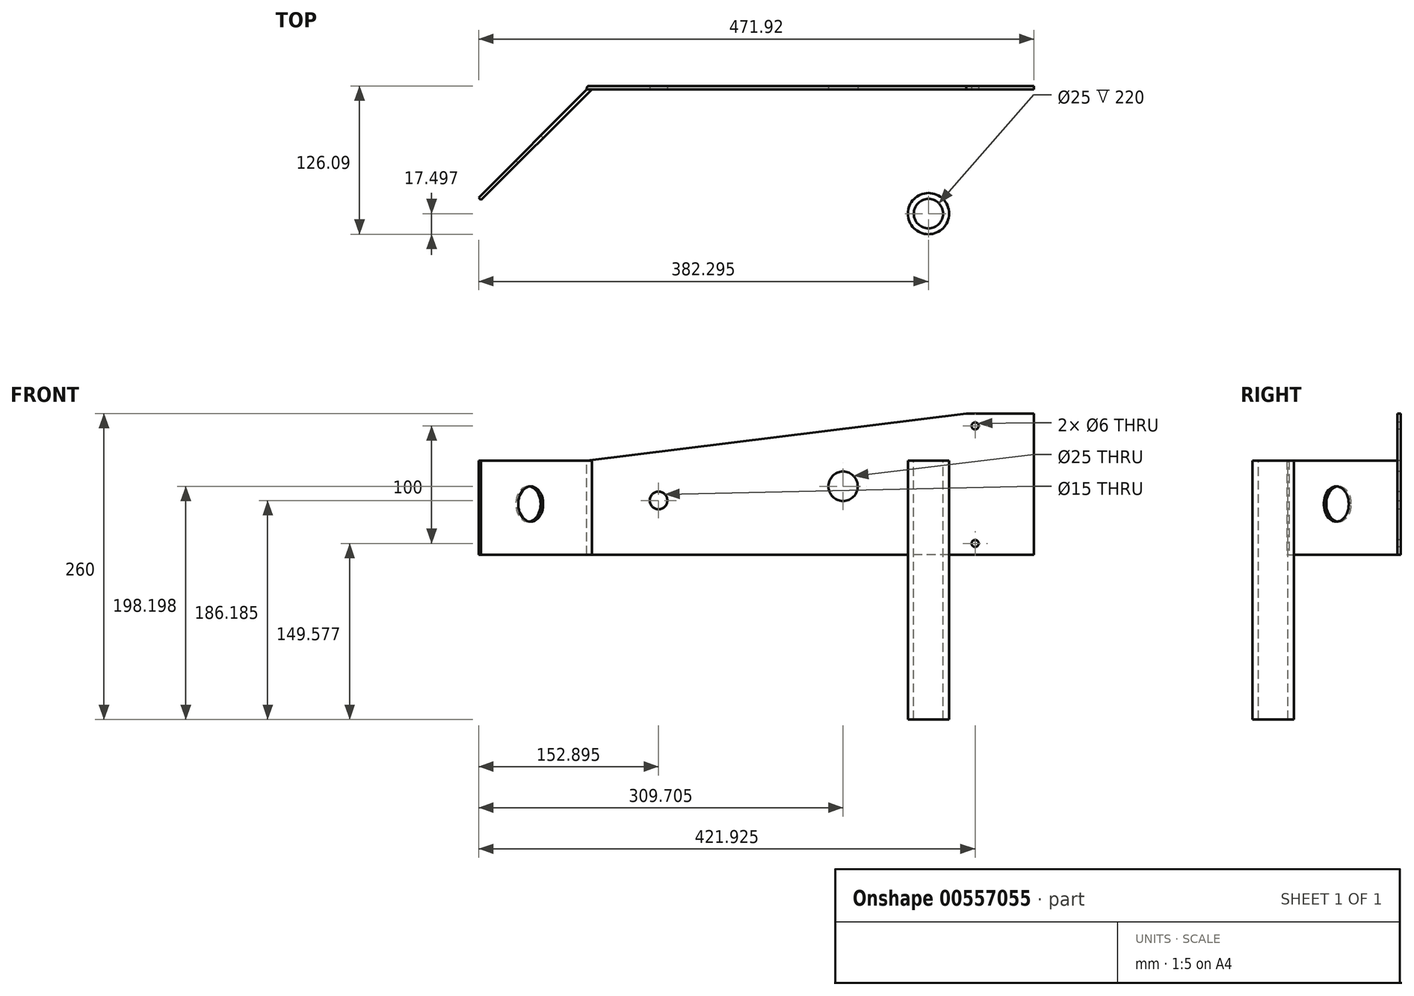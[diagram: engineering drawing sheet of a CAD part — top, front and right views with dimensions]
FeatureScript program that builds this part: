
annotation { "Feature Type Name" : "Feature", "Feature Type Description" : "" }
export const myFeature = defineFeature(function(context is Context, id is Id, definition is map)
    precondition{}
    {
        {
            var Q0;
            Q0=qCreatedBy(makeId("Front.planeOp"),FACE);
            var sketch = newSketch(context, id + "F0", { "sketchPlane" : qUnion([Q0])});
            skLineSegment(sketch, "E0.bottom", {"start": v(286.31, -3.5) * mm, "end": v(-93.69, -3.5) * mm});
            skLineSegment(sketch, "E0.top", {"start": v(286.31, 116.5) * mm, "end": v(228.84, 116.5) * mm});
            skLineSegment(sketch, "E0.left", {"start": v(286.31, -3.5) * mm, "end": v(286.31, 116.5) * mm});
            skLineSegment(sketch, "E0.right", {"start": v(-93.69, -3.5) * mm, "end": v(-93.69, 76.5) * mm});
            skLineSegment(sketch, "E1", {"start": v(-93.69, 76.5) * mm, "end": v(228.84, 116.5) * mm});
            skSolve(sketch);
        }
        {
            var Q0;
            Q0=makeQuery(id+"F0.imprint","IMPRINT",FACE,{"disambiguationData":[TD([[makeQuery(id+"F0.imprint","IMPRINT",EDGE,{"derivedFrom":sQuery(id+"F0.wireOp",EDGE,"E0.bottom")}),-1.0]])]});
            extrude(context, id + "F1", {"entities" : qUnion([Q0]), "depth" : 3 * mm, "offsetDistance" : 25 * mm});
        }
        {
            var Q0;
            Q0=makeQuery(id+"F1.opExtrude","SWEPT_FACE",FACE,{"disambiguationData":[OSD([sQuery(id+"F0.wireOp",EDGE,"E0.bottom")])]});
            var sketch = newSketch(context, id + "F2", { "sketchPlane" : qUnion([Q0])});
            skLineSegment(sketch, "E2", {"start": v(-93.69, 3) * mm, "end": v(-185.6, 94.92) * mm});
            skLineSegment(sketch, "E3", {"start": v(-185.6, 94.92) * mm, "end": v(-183.49, 97.05) * mm});
            skLineSegment(sketch, "E4", {"start": v(-183.49, 97.05) * mm, "end": v(-86.44, 0) * mm});
            skLineSegment(sketch, "E5", {"start": v(-93.69, 3) * mm, "end": v(-217, 3) * mm, "construction": true});
            skSolve(sketch);
        }
        {
            var Q0;
            {var subQ0=sQuery(id+"F2.wireOp",EDGE,"E2");Q0=makeQuery(id+"F2.imprint","IMPRINT",FACE,{"disambiguationData":[TD([[makeQuery(id+"F2.imprint","IMPRINT",EDGE,{"derivedFrom":subQ0}),-1.0]])]});}
            var sketch = newSketch(context, id + "F3", { "sketchPlane" : qUnion([Q0])});
            skSolve(sketch);
        }
        {
            var Q0;
            {var subQ0=sQuery(id+"F2.wireOp",EDGE,"E2");Q0=makeQuery(id+"F2.imprint","IMPRINT",FACE,{"disambiguationData":[TD([[makeQuery(id+"F2.imprint","IMPRINT",EDGE,{"derivedFrom":subQ0}),-1.0]])]});}
            extrude(context, id + "F4", {"entities" : qUnion([Q0]), "operationType" : NewBodyOperationType.ADD, "oppositeDirection" : true, "depth" : 80 * mm, "offsetDistance" : 25 * mm});
        }
        {
            var Q0;
            Q0=makeQuery(id+"F1.opExtrude","CAP_EDGE",EDGE,{"disambiguationData":[OSD([sQuery(id+"F0.wireOp",EDGE,"E0.right")])],"isStart":true});
            fillet(context, id + "F5", {"entities" : qUnion([Q0]), "radius" : 2 * mm, "tangentPropagation" : true, "allowEdgeOverflow" : false});
        }
        {
            var Q0;
            {var subQ0=sQuery(id+"F2.wireOp",EDGE,"E2");Q0=makeQuery(id+"F3.imprint","IMPRINT",FACE,{"disambiguationData":[TD([[makeQuery(id+"F3.imprint","IMPRINT",EDGE,{"derivedFrom":makeQuery(id+"F2.imprint","IMPRINT",EDGE,{"derivedFrom":subQ0})}),-1.0]])]});}
            extrude(context, id + "F6", {"entities" : qUnion([Q0]), "oppositeDirection" : true, "depth" : 80 * mm, "offsetDistance" : 25 * mm});
        }
        {
            var Q0;
            Q0=makeQuery(id+"F1.opExtrude","CAP_FACE",FACE,{"disambiguationData":[OSD([sQuery(id+"F0.wireOp",EDGE,"E0.bottom"),sQuery(id+"F0.wireOp",EDGE,"E0.top"),sQuery(id+"F0.wireOp",EDGE,"E0.left"),sQuery(id+"F0.wireOp",EDGE,"E0.right"),sQuery(id+"F0.wireOp",EDGE,"E1")])],"isStart":false});
            var sketch = newSketch(context, id + "F7", { "sketchPlane" : qUnion([Q0])});
            skCircle(sketch, "E6", {"center": v(124.1, 54.7) * mm, "radius": 12.5 * mm});
            skSolve(sketch);
        }
        {
            var Q0;
            Q0=makeQuery(id+"F7.imprint","IMPRINT",FACE,{"disambiguationData":[TD([[makeQuery(id+"F7.imprint","IMPRINT",EDGE,{"derivedFrom":sQuery(id+"F7.wireOp",EDGE,"E6")}),1.0]])]});
            extrude(context, id + "F8", {"entities" : qUnion([Q0]), "operationType" : NewBodyOperationType.REMOVE, "oppositeDirection" : true, "depth" : 3 * mm, "offsetDistance" : 25 * mm});
        }
        {
            var Q0;
            Q0=makeQuery(id+"F1.opExtrude","CAP_FACE",FACE,{"disambiguationData":[OSD([sQuery(id+"F0.wireOp",EDGE,"E0.bottom"),sQuery(id+"F0.wireOp",EDGE,"E0.top"),sQuery(id+"F0.wireOp",EDGE,"E0.left"),sQuery(id+"F0.wireOp",EDGE,"E0.right"),sQuery(id+"F0.wireOp",EDGE,"E1")])],"isStart":false});
            var sketch = newSketch(context, id + "F9", { "sketchPlane" : qUnion([Q0])});
            skCircle(sketch, "E7", {"center": v(-32.71, 42.7) * mm, "radius": 7.5 * mm});
            skSolve(sketch);
        }
        {
            var Q0;
            Q0=makeQuery(id+"F9.imprint","IMPRINT",FACE,{"disambiguationData":[TD([[makeQuery(id+"F9.imprint","IMPRINT",EDGE,{"derivedFrom":sQuery(id+"F9.wireOp",EDGE,"E7")}),1.0]])]});
            extrude(context, id + "F10", {"entities" : qUnion([Q0]), "operationType" : NewBodyOperationType.REMOVE, "endBound" : BoundingType.THROUGH_ALL, "oppositeDirection" : true, "depth" : 3 * mm, "offsetDistance" : 25 * mm});
        }
        {
            var Q0;
            Q0=makeQuery(id+"F1.opExtrude","CAP_FACE",FACE,{"disambiguationData":[OSD([sQuery(id+"F0.wireOp",EDGE,"E0.bottom"),sQuery(id+"F0.wireOp",EDGE,"E0.top"),sQuery(id+"F0.wireOp",EDGE,"E0.left"),sQuery(id+"F0.wireOp",EDGE,"E0.right"),sQuery(id+"F0.wireOp",EDGE,"E1")])],"isStart":false});
            var sketch = newSketch(context, id + "F11", { "sketchPlane" : qUnion([Q0])});
            skLineSegment(sketch, "E8", {"start": v(-33, 35.2) * mm, "end": v(124.65, 42.22) * mm});
            skLineSegment(sketch, "E9", {"start": v(-33.27, 50.17) * mm, "end": v(125.22, 67.4) * mm});
            skSolve(sketch);
        }
        {
            var Q0;
            {var subQ0=sQuery(id+"F11.wireOp",EDGE,"E8");var subQ1=makeQuery(id+"F8.boolean.opBoolean","COPY",EDGE,{"derivedFrom":makeQuery(id+"F8.opExtrude","CAP_EDGE",EDGE,{"disambiguationData":[OSD([sQuery(id+"F7.wireOp",EDGE,"E6")])],"isStart":true})});var subQ2=makeQuery(id+"F11.imprint","INTERSECT",VERTEX,{"derivedFrom":[subQ1,subQ0]});Q0=makeQuery(id+"F11.imprint","IMPRINT",FACE,{"disambiguationData":[TD([[makeQuery(id+"F11.imprint","IMPRINT",EDGE,{"disambiguationData":[TD([[subQ2,1.0]])],"derivedFrom":subQ0}),1.0]])]});}
            extrude(context, id + "F12", {"entities" : qUnion([Q0]), "operationType" : NewBodyOperationType.REMOVE, "oppositeDirection" : true, "depth" : 3 * mm, "offsetDistance" : 25 * mm});
        }
        {
            var Q0;
            Q0=makeQuery(id+"F4.opExtrude","SWEPT_FACE",FACE,{"disambiguationData":[OSD([sQuery(id+"F2.wireOp",EDGE,"E4")])]});
            var sketch = newSketch(context, id + "F13", { "sketchPlane" : qUnion([Q0])});
            skCircle(sketch, "E10", {"center": v(-138.84, 39.67) * mm, "radius": 15 * mm});
            skSolve(sketch);
        }
        {
            var Q0;
            Q0=makeQuery(id+"F1.opExtrude","CAP_FACE",FACE,{"disambiguationData":[OSD([sQuery(id+"F0.wireOp",EDGE,"E0.bottom"),sQuery(id+"F0.wireOp",EDGE,"E0.top"),sQuery(id+"F0.wireOp",EDGE,"E0.left"),sQuery(id+"F0.wireOp",EDGE,"E0.right"),sQuery(id+"F0.wireOp",EDGE,"E1")])],"isStart":false});
            var sketch = newSketch(context, id + "F14", { "sketchPlane" : qUnion([Q0])});
            skLineSegment(sketch, "E11", {"start": v(286.31, 116.5) * mm, "end": v(236.31, 116.5) * mm});
            skLineSegment(sketch, "E12", {"start": v(236.31, 116.5) * mm, "end": v(236.31, 106.09) * mm});
            skCircle(sketch, "E13", {"center": v(236.31, 106.09) * mm, "radius": 3 * mm});
            skSolve(sketch);
        }
        {
            var Q0;
            Q0=makeQuery(id+"F14.imprint","IMPRINT",FACE,{"disambiguationData":[TD([[makeQuery(id+"F14.imprint","IMPRINT",EDGE,{"derivedFrom":sQuery(id+"F14.wireOp",EDGE,"E13")}),1.0]])]});
            extrude(context, id + "F15", {"entities" : qUnion([Q0]), "operationType" : NewBodyOperationType.REMOVE, "endBound" : BoundingType.THROUGH_ALL, "oppositeDirection" : true, "depth" : 3 * mm, "offsetDistance" : 25 * mm});
        }
        {
            var Q0;
            Q0=makeQuery(id+"F1.opExtrude","CAP_FACE",FACE,{"disambiguationData":[OSD([sQuery(id+"F0.wireOp",EDGE,"E0.bottom"),sQuery(id+"F0.wireOp",EDGE,"E0.top"),sQuery(id+"F0.wireOp",EDGE,"E0.left"),sQuery(id+"F0.wireOp",EDGE,"E0.right"),sQuery(id+"F0.wireOp",EDGE,"E1")])],"isStart":false});
            var sketch = newSketch(context, id + "F16", { "sketchPlane" : qUnion([Q0])});
            skLineSegment(sketch, "E14", {"start": v(236.31, 106.09) * mm, "end": v(236.31, 6.09) * mm});
            skCircle(sketch, "E15", {"center": v(236.31, 6.09) * mm, "radius": 3 * mm});
            skSolve(sketch);
        }
        {
            var Q0;
            Q0=makeQuery(id+"F16.imprint","IMPRINT",FACE,{"disambiguationData":[TD([[makeQuery(id+"F16.imprint","IMPRINT",EDGE,{"derivedFrom":sQuery(id+"F16.wireOp",EDGE,"E15")}),1.0]])]});
            extrude(context, id + "F17", {"entities" : qUnion([Q0]), "operationType" : NewBodyOperationType.REMOVE, "endBound" : BoundingType.THROUGH_ALL, "oppositeDirection" : true, "depth" : 25 * mm, "offsetDistance" : 25 * mm});
        }
        {
            var Q0;
            {var subQ0=sQuery(id+"F2.wireOp",EDGE,"E2");Q0=makeQuery(id+"F2.imprint","IMPRINT",FACE,{"disambiguationData":[TD([[makeQuery(id+"F2.imprint","IMPRINT",EDGE,{"derivedFrom":subQ0}),-1.0]])]});}
            extrude(context, id + "F18", {"entities" : qUnion([Q0]), "operationType" : NewBodyOperationType.ADD, "oppositeDirection" : true, "depth" : 80 * mm, "offsetDistance" : 25 * mm});
        }
        {
            var Q0;
            Q0=makeQuery(id+"F13.imprint","IMPRINT",FACE,{"disambiguationData":[TD([[makeQuery(id+"F13.imprint","IMPRINT",EDGE,{"derivedFrom":sQuery(id+"F13.wireOp",EDGE,"E10")}),1.0]])]});
            extrude(context, id + "F19", {"entities" : qUnion([Q0]), "operationType" : NewBodyOperationType.REMOVE, "endBound" : BoundingType.THROUGH_ALL, "oppositeDirection" : true, "depth" : 25 * mm, "offsetDistance" : 25 * mm});
        }
        {
            var Q0;
            Q0=makeQuery(id+"F4.opExtrude","CAP_FACE",FACE,{"disambiguationData":[OSD([sQuery(id+"F0.wireOp",EDGE,"E0.bottom"),sQuery(id+"F2.wireOp",EDGE,"E2"),sQuery(id+"F2.wireOp",EDGE,"E3"),sQuery(id+"F2.wireOp",EDGE,"E4")])],"isStart":false});
            var sketch = newSketch(context, id + "F20", { "sketchPlane" : qUnion([Q0])});
            skCircle(sketch, "E16", {"center": v(-196.68, -108.6) * mm, "radius": 17.5 * mm});
            skSolve(sketch);
        }
        {
            var Q0;
            Q0=makeQuery(id+"F20.imprint","IMPRINT",FACE,{"disambiguationData":[TD([[makeQuery(id+"F20.imprint","IMPRINT",EDGE,{"derivedFrom":sQuery(id+"F20.wireOp",EDGE,"E16")}),1.0]])]});
            extrude(context, id + "F21", {"entities" : qUnion([Q0]), "oppositeDirection" : true, "depth" : 220 * mm, "offsetDistance" : 25 * mm});
        }
        {
            var Q0;
            Q0=makeQuery(id+"F21.opExtrude","CAP_FACE",FACE,{"disambiguationData":[OSD([sQuery(id+"F20.wireOp",EDGE,"E16")])],"isStart":true});
            var sketch = newSketch(context, id + "F22", { "sketchPlane" : qUnion([Q0])});
            skCircle(sketch, "E17", {"center": v(-196.68, -108.6) * mm, "radius": 12.5 * mm});
            skSolve(sketch);
        }
        {
            var Q0;
            Q0=makeQuery(id+"F22.imprint","IMPRINT",FACE,{"disambiguationData":[TD([[makeQuery(id+"F22.imprint","IMPRINT",EDGE,{"derivedFrom":sQuery(id+"F22.wireOp",EDGE,"E17")}),1.0]])]});
            extrude(context, id + "F23", {"entities" : qUnion([Q0]), "operationType" : NewBodyOperationType.REMOVE, "endBound" : BoundingType.THROUGH_ALL, "oppositeDirection" : true, "depth" : 220 * mm, "offsetDistance" : 25 * mm});
        }
        {
            var Q0;
            Q0=makeQuery(id+"F21.opExtrude","SWEPT_BODY",BODY,{"disambiguationData":[OSD([sQuery(id+"F20.wireOp",EDGE,"E16")])]});
            var Q1;
            Q1=qCreatedBy(makeId("Right.planeOp"),FACE);
            mirror(context, id + "F24", {"entities" : qUnion([Q0]), "mirrorPlane" : qUnion([Q1])});
        }
        {
            var Q0;
            Q0=makeQuery(id+"F21.opExtrude","SWEPT_BODY",BODY,{"disambiguationData":[OSD([sQuery(id+"F20.wireOp",EDGE,"E16")])]});
            deleteBodies(context, id + "F25", {"entities" : qUnion([Q0])});
        }
    });
